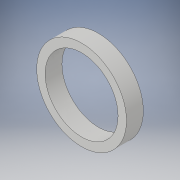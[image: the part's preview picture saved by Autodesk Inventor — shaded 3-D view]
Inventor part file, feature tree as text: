
AUTODESK INVENTOR PART (.ipt)
format: ipt  version: 2019 (Build 230136000, 136)  size: 103,936 bytes
history: native  units: mm
features: extrude x2, sketch x2
ambient origin geometry x8: Origin, YZ Plane, XZ Plane, XY Plane, X Axis, Y Axis, Z Axis, Center Point
bodies: Solid1 (feature_tree)
feature tree (4):
  extrude  "Extrusion1"  Depth=60.0mm TaperAngle=0.0deg
  extrude  "Extrusion2"  Depth=6.0mm TaperAngle=0.0deg
  sketch  "Sketch1"  dims[d0=320.0mm d1=60.0mm d2=0.0mm]
  sketch  "Sketch2"  dims[d3=260.0mm d4=6.0mm d5=0.0mm]
